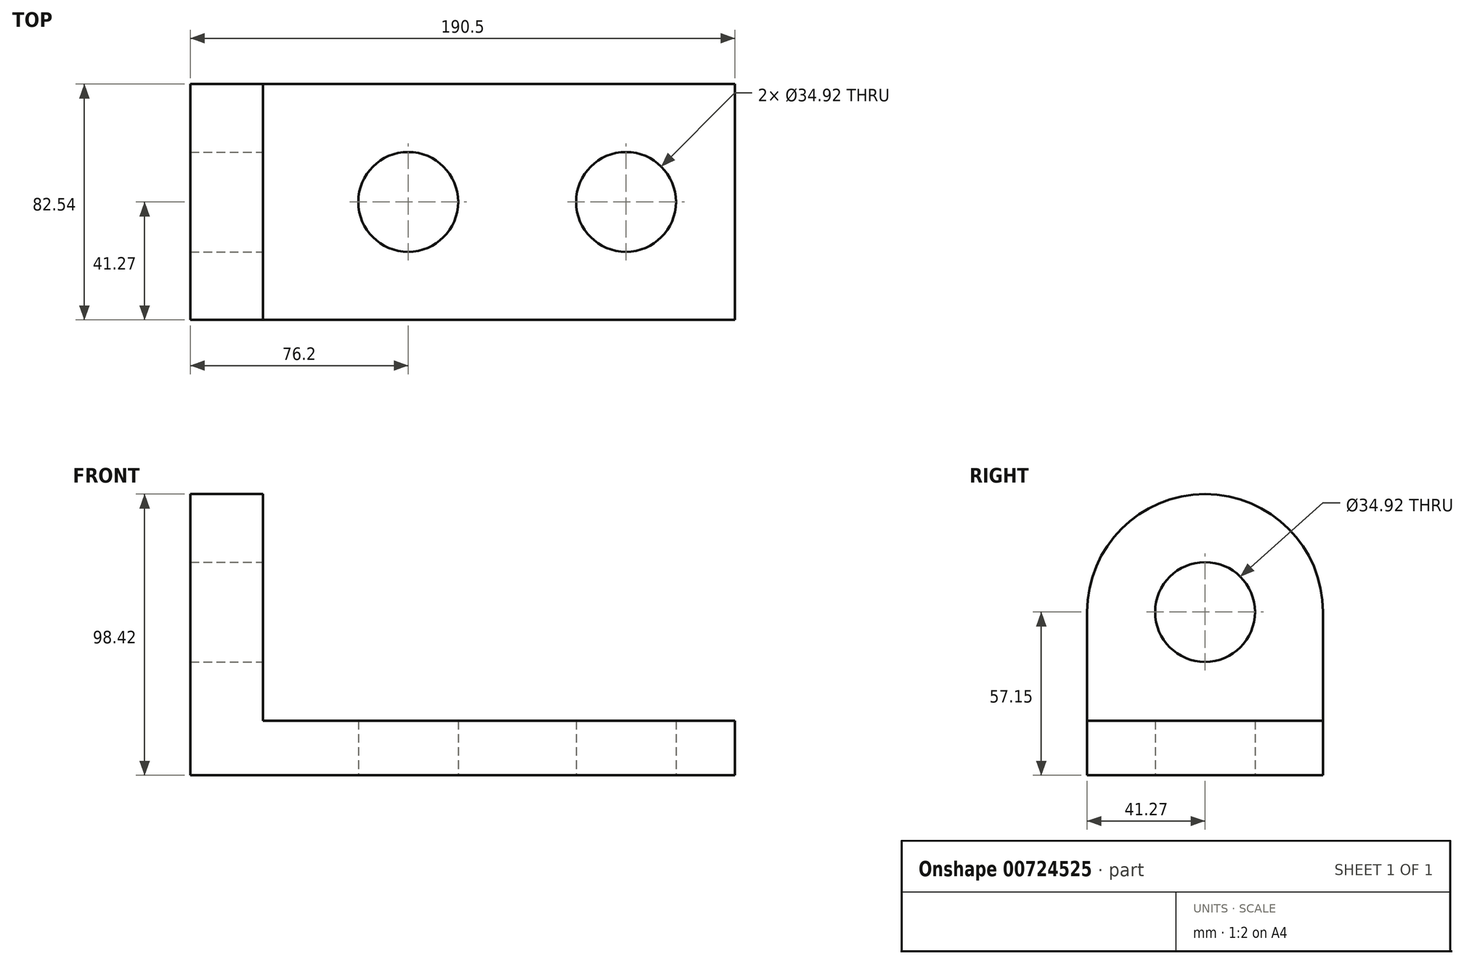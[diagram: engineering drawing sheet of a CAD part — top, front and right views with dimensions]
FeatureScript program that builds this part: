
annotation { "Feature Type Name" : "Feature", "Feature Type Description" : "" }
export const myFeature = defineFeature(function(context is Context, id is Id, definition is map)
    precondition{}
    {
        {
            var Q0;
            Q0=qCreatedBy(makeId("Top.planeOp"),FACE);
            var sketch = newSketch(context, id + "F0", { "sketchPlane" : qUnion([Q0])});
            skLineSegment(sketch, "E0.bottom", {"start": v(95.25, 41.28) * mm, "end": v(-95.25, 41.27) * mm});
            skLineSegment(sketch, "E0.top", {"start": v(95.25, -41.27) * mm, "end": v(-95.25, -41.28) * mm});
            skLineSegment(sketch, "E0.left", {"start": v(95.25, 41.28) * mm, "end": v(95.25, -41.27) * mm});
            skLineSegment(sketch, "E0.right", {"start": v(-95.25, 41.27) * mm, "end": v(-95.25, -41.28) * mm});
            skPoint(sketch, "E0.middle", {"position": v(0, 0) * mm});
            skLineSegment(sketch, "E1", {"start": v(-69.85, 41.27) * mm, "end": v(-69.85, -41.28) * mm});
            skCircle(sketch, "E2", {"center": v(-19.05, 0) * mm, "radius": 17.46 * mm});
            skCircle(sketch, "E3", {"center": v(57.15, 0) * mm, "radius": 17.46 * mm});
            skSolve(sketch);
        }
        {
            var Q0;
            Q0=qSketchRegion(id+"F0",true);
            extrude(context, id + "F1", {"entities" : qUnion([Q0]), "depth" : 19.05 * mm});
        }
        {
            var Q0;
            {var subQ0=sQuery(id+"F0.wireOp",EDGE,"E0.right");Q0=makeQuery(id+"F0.imprint","IMPRINT",FACE,{"disambiguationData":[TD([[makeQuery(id+"F0.imprint","IMPRINT",EDGE,{"derivedFrom":subQ0}),1.0]])]});}
            extrude(context, id + "F2", {"entities" : qUnion([Q0]), "operationType" : NewBodyOperationType.ADD, "depth" : 57.15 * mm});
        }
        {
            var Q0;
            Q0=makeQuery(id+"F2.opExtrude","SWEPT_FACE",FACE,{"disambiguationData":[OSD([sQuery(id+"F0.wireOp",EDGE,"E1")])]});
            var sketch = newSketch(context, id + "F3", { "sketchPlane" : qUnion([Q0])});
            skCircle(sketch, "E4", {"center": v(0, 57.15) * mm, "radius": 17.46 * mm});
            skArc(sketch, "E5", {"start": v(41.28, 57.15) * mm, "mid": v(0, 98.43) * mm, "end": v(-41.28, 57.15) * mm});
            skSolve(sketch);
        }
        {
            var Q0;
            {var subQ5=sQuery(id+"F3.wireOp",EDGE,"E5");Q0=makeQuery(id+"F3.imprint","IMPRINT",FACE,{"disambiguationData":[TD([[makeQuery(id+"F3.imprint","IMPRINT",EDGE,{"derivedFrom":subQ5}),1.0]])]});}
            extrude(context, id + "F4", {"entities" : qUnion([Q0]), "operationType" : NewBodyOperationType.ADD, "oppositeDirection" : true, "depth" : 25.4 * mm});
        }
        {
            var Q0;
            Q0=qSketchRegion(id+"F3",true);
            extrude(context, id + "F5", {"entities" : qUnion([Q0]), "operationType" : NewBodyOperationType.REMOVE, "oppositeDirection" : true, "depth" : 25.4 * mm});
        }
    });
